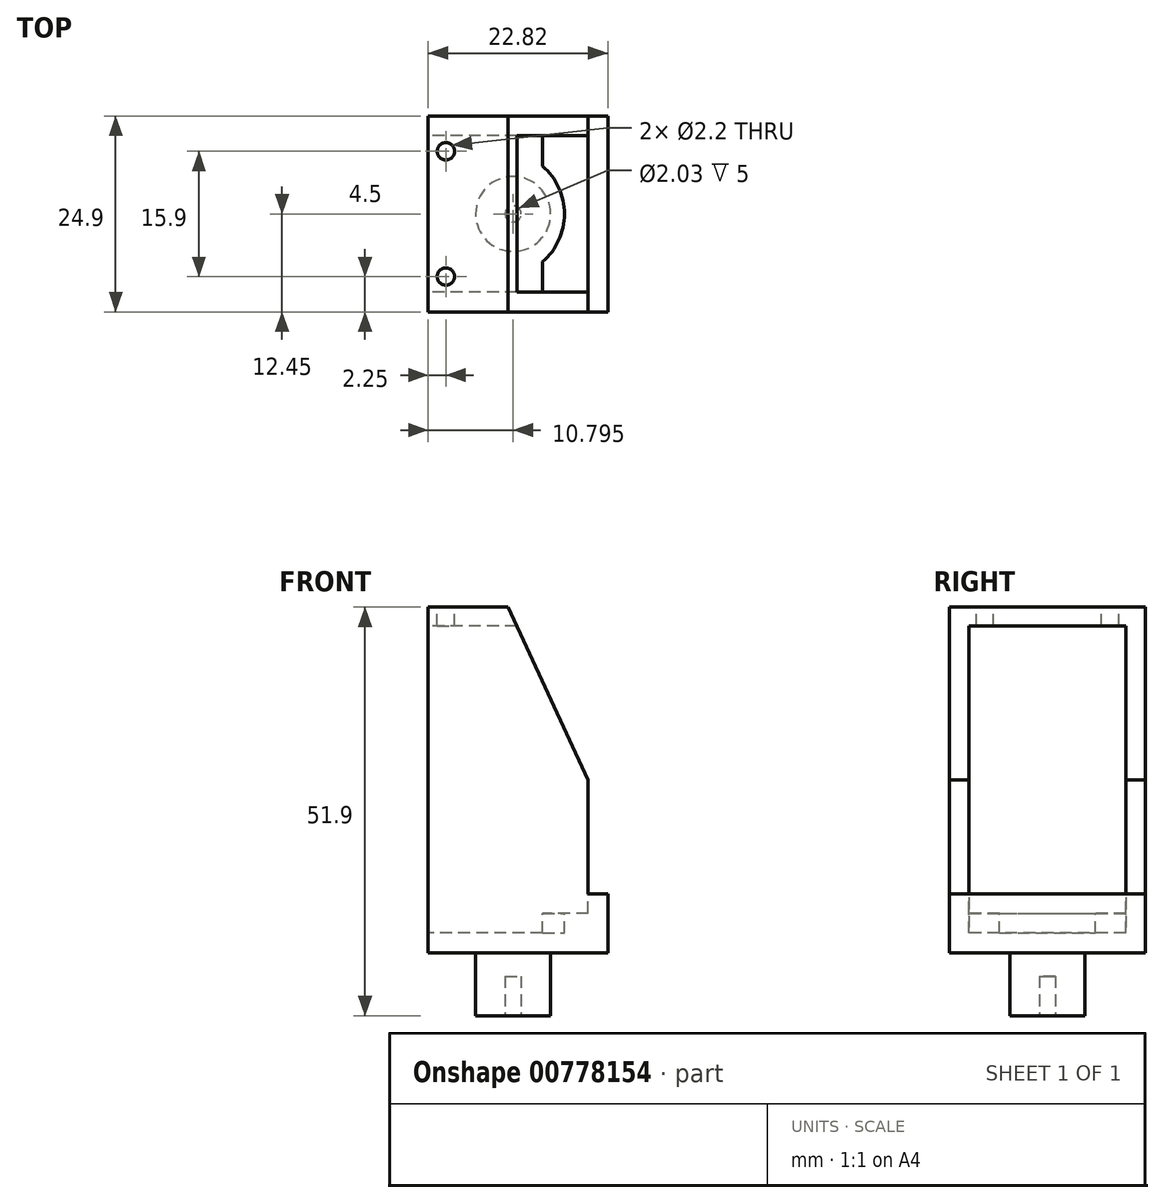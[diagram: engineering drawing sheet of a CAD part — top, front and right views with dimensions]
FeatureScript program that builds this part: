
annotation { "Feature Type Name" : "Feature", "Feature Type Description" : "" }
export const myFeature = defineFeature(function(context is Context, id is Id, definition is map)
    precondition{}
    {
        {
            var Q0;
            Q0=qCreatedBy(makeId("Front.planeOp"),FACE);
            var sketch = newSketch(context, id + "F0", { "sketchPlane" : qUnion([Q0])});
            skLineSegment(sketch, "E0.bottom", {"start": v(0, 21.95) * mm, "end": v(-10.16, 21.95) * mm});
            skLineSegment(sketch, "E0.top", {"start": v(10.16, -21.95) * mm, "end": v(-10.16, -21.95) * mm});
            skLineSegment(sketch, "E0.left", {"start": v(10.16, 0) * mm, "end": v(10.16, -21.95) * mm});
            skLineSegment(sketch, "E0.right", {"start": v(-10.16, 21.95) * mm, "end": v(-10.16, -21.95) * mm});
            skPoint(sketch, "E0.middle", {"position": v(0, 0) * mm});
            skLineSegment(sketch, "E1", {"start": v(0, 21.95) * mm, "end": v(10.16, 0) * mm});
            skPoint(sketch, "E2.orphan", {"position": v(10.16, 21.95) * mm});
            skSolve(sketch);
        }
        {
            var Q0;
            Q0 = qSketchRegion(id + "F0", true);
            extrude(context, id + "F1", {"entities" : qUnion([Q0]), "depth" : 24.9 * mm, "offsetDistance" : 25.4 * mm});
        }
        {
            var Q0;
            Q0=makeQuery(id+"F1.opExtrude","SWEPT_FACE",FACE,{"disambiguationData":[OSD([sQuery(id+"F0.wireOp",EDGE,"E0.right")])]});
            var sketch = newSketch(context, id + "F2", { "sketchPlane" : qUnion([Q0])});
            skLineSegment(sketch, "E3.bottom", {"start": v(2.5, 19.55) * mm, "end": v(22.4, 19.55) * mm});
            skLineSegment(sketch, "E3.top", {"start": v(2.5, -16.95) * mm, "end": v(22.4, -16.95) * mm});
            skLineSegment(sketch, "E3.left", {"start": v(2.5, 19.55) * mm, "end": v(2.5, -16.95) * mm});
            skLineSegment(sketch, "E3.right", {"start": v(22.4, 19.55) * mm, "end": v(22.4, -16.95) * mm});
            skSolve(sketch);
        }
        {
            var Q0;
            Q0 = qSketchRegion(id + "F2", true);
            extrude(context, id + "F3", {"entities" : qUnion([Q0]), "operationType" : NewBodyOperationType.REMOVE, "oppositeDirection" : true, "depth" : 25.4 * mm, "offsetDistance" : 25.4 * mm});
        }
        {
            var Q0;
            Q0=makeQuery(id+"F1.opExtrude","SWEPT_FACE",FACE,{"disambiguationData":[OSD([sQuery(id+"F0.wireOp",EDGE,"E0.right")])]});
            var sketch = newSketch(context, id + "F4", { "sketchPlane" : qUnion([Q0])});
            skLineSegment(sketch, "E4.bottom", {"start": v(0, 21.95) * mm, "end": v(24.9, 21.95) * mm});
            skLineSegment(sketch, "E4.top", {"start": v(0, 16.95) * mm, "end": v(24.9, 16.95) * mm});
            skLineSegment(sketch, "E4.left", {"start": v(0, 21.95) * mm, "end": v(0, 16.95) * mm});
            skLineSegment(sketch, "E4.right", {"start": v(24.9, 21.95) * mm, "end": v(24.9, 16.95) * mm});
            skLineSegment(sketch, "E5.bottom", {"start": v(0, -21.95) * mm, "end": v(24.9, -21.95) * mm});
            skLineSegment(sketch, "E5.top", {"start": v(0, -14.45) * mm, "end": v(24.9, -14.45) * mm});
            skLineSegment(sketch, "E5.left", {"start": v(0, -21.95) * mm, "end": v(0, -14.45) * mm});
            skLineSegment(sketch, "E5.right", {"start": v(24.9, -21.95) * mm, "end": v(24.9, -14.45) * mm});
            skSolve(sketch);
        }
        {
            var Q0;
            Q0 = qSketchRegion(id + "F4", true);
            extrude(context, id + "F5", {"entities" : qUnion([Q0]), "operationType" : NewBodyOperationType.ADD, "depth" : 2.5 * mm, "offsetDistance" : 25.4 * mm});
        }
        {
            var Q0;
            Q0=makeQuery(id+"F3.boolean.opBoolean","COPY",FACE,{"derivedFrom":makeQuery(id+"F3.opExtrude","SWEPT_FACE",FACE,{"disambiguationData":[OSD([sQuery(id+"F2.wireOp",EDGE,"E3.top")])]})});
            var sketch = newSketch(context, id + "F6", { "sketchPlane" : qUnion([Q0])});
            skLineSegment(sketch, "E6.bottom", {"start": v(10.16, -2.5) * mm, "end": v(4.36, -2.5) * mm});
            skLineSegment(sketch, "E6.top", {"start": v(10.16, -22.4) * mm, "end": v(4.36, -22.4) * mm});
            skLineSegment(sketch, "E6.left", {"start": v(10.16, -2.5) * mm, "end": v(10.16, -22.4) * mm});
            skLineSegment(sketch, "E6.right", {"start": v(4.36, -2.5) * mm, "end": v(4.36, -6.37) * mm});
            skPoint(sketch, "E7", {"position": v(-0.84, -12.45) * mm});
            skPoint(sketch, "E7.positionSnap0", {"position": v(4.36, -12.45) * mm});
            skArc(sketch, "E8", {"start": v(4.36, -6.37) * mm, "mid": v(7.16, -12.45) * mm, "end": v(4.36, -18.53) * mm});
            skLineSegment(sketch, "E9.trimOffspring", {"start": v(4.36, -18.53) * mm, "end": v(4.36, -22.4) * mm});
            skSolve(sketch);
        }
        {
            var Q0;
            {var subQ3=sQuery(id+"F6.wireOp",EDGE,"E6.right");Q0=makeQuery(id+"F6.imprint","IMPRINT",FACE,{"disambiguationData":[TD([[makeQuery(id+"F6.imprint","IMPRINT",EDGE,{"derivedFrom":subQ3}),-1.0]])]});}
            extrude(context, id + "F7", {"entities" : qUnion([Q0]), "operationType" : NewBodyOperationType.REMOVE, "oppositeDirection" : true, "depth" : 2.5 * mm, "offsetDistance" : 25.4 * mm});
        }
        {
            var Q0;
            Q0=makeQuery(id+"F5.boolean.opBoolean","MERGE",FACE,{"derivedFrom":[makeQuery(id+"F1.opExtrude","SWEPT_FACE",FACE,{"disambiguationData":[OSD([sQuery(id+"F0.wireOp",EDGE,"E0.bottom")])]}),makeQuery(id+"F5.opExtrude","SWEPT_FACE",FACE,{"disambiguationData":[OSD([sQuery(id+"F4.wireOp",EDGE,"E4.bottom")])]})]});
            var sketch = newSketch(context, id + "F8", { "sketchPlane" : qUnion([Q0])});
            skCircle(sketch, "E10", {"center": v(-7.9, -4.5) * mm, "radius": 1.1 * mm});
            skLineSegment(sketch, "E11", {"start": v(-31.79, -12.45) * mm, "end": v(21.26, -12.45) * mm, "construction": true});
            skPoint(sketch, "E11.startSnap0", {"position": v(-12.66, -12.45) * mm});
            skCircle(sketch, "E12.MirrorC", {"center": v(-7.9, -20.4) * mm, "radius": 1.1 * mm});
            skSolve(sketch);
        }
        {
            var Q0;
            Q0 = qSketchRegion(id + "F8", true);
            extrude(context, id + "F9", {"entities" : qUnion([Q0]), "operationType" : NewBodyOperationType.REMOVE, "oppositeDirection" : true, "depth" : 25.4 * mm, "offsetDistance" : 25.4 * mm});
        }
        {
            var Q0;
            Q0=makeQuery(id+"F5.boolean.opBoolean","MERGE",FACE,{"derivedFrom":[makeQuery(id+"F1.opExtrude","SWEPT_FACE",FACE,{"disambiguationData":[OSD([sQuery(id+"F0.wireOp",EDGE,"E0.top")])]}),makeQuery(id+"F5.opExtrude","SWEPT_FACE",FACE,{"disambiguationData":[OSD([sQuery(id+"F4.wireOp",EDGE,"E5.bottom")])]})]});
            var sketch = newSketch(context, id + "F10", { "sketchPlane" : qUnion([Q0])});
            skCircle(sketch, "E13", {"center": v(0.64, 12.45) * mm, "radius": 4.76 * mm});
            skLineSegment(sketch, "E14", {"start": v(-12.66, 12.45) * mm, "end": v(10.16, 12.45) * mm, "construction": true});
            skSolve(sketch);
        }
        {
            var Q0;
            Q0 = qSketchRegion(id + "F10", true);
            extrude(context, id + "F11", {"entities" : qUnion([Q0]), "operationType" : NewBodyOperationType.ADD, "depth" : 8 * mm, "offsetDistance" : 25.4 * mm});
        }
        {
            var Q0;
            Q0=makeQuery(id+"F11.opExtrude","CAP_FACE",FACE,{"disambiguationData":[OSD([sQuery(id+"F10.wireOp",EDGE,"E13")])],"isStart":false});
            var sketch = newSketch(context, id + "F12", { "sketchPlane" : qUnion([Q0])});
            skCircle(sketch, "E15", {"center": v(0.64, 12.45) * mm, "radius": 1.02 * mm});
            skSolve(sketch);
        }
        {
            var Q0;
            Q0 = qSketchRegion(id + "F12", true);
            extrude(context, id + "F13", {"entities" : qUnion([Q0]), "operationType" : NewBodyOperationType.REMOVE, "oppositeDirection" : true, "depth" : 5 * mm, "offsetDistance" : 25.4 * mm});
        }
        {
            var Q0;
            Q0=makeQuery(id+"F5.boolean.opBoolean","MERGE",FACE,{"derivedFrom":[makeQuery(id+"F1.opExtrude","CAP_FACE",FACE,{"disambiguationData":[OSD([sQuery(id+"F0.wireOp",EDGE,"E0.bottom"),sQuery(id+"F0.wireOp",EDGE,"E0.top"),sQuery(id+"F0.wireOp",EDGE,"E0.left"),sQuery(id+"F0.wireOp",EDGE,"E0.right"),sQuery(id+"F0.wireOp",EDGE,"E1")])],"isStart":false}),makeQuery(id+"F5.opExtrude","SWEPT_FACE",FACE,{"disambiguationData":[OSD([sQuery(id+"F4.wireOp",EDGE,"E4.right")])]}),makeQuery(id+"F5.opExtrude","SWEPT_FACE",FACE,{"disambiguationData":[OSD([sQuery(id+"F4.wireOp",EDGE,"E5.right")])]})]});
            var sketch = newSketch(context, id + "F14", { "sketchPlane" : qUnion([Q0])});
            skLineSegment(sketch, "E16.bottom", {"start": v(-12.66, -14.45) * mm, "end": v(-10.16, -14.45) * mm});
            skLineSegment(sketch, "E16.top", {"start": v(-12.66, -21.95) * mm, "end": v(-10.16, -21.95) * mm});
            skLineSegment(sketch, "E16.left", {"start": v(-12.66, -14.45) * mm, "end": v(-12.66, -21.95) * mm});
            skLineSegment(sketch, "E16.right", {"start": v(-10.16, -14.45) * mm, "end": v(-10.16, -21.95) * mm});
            skLineSegment(sketch, "E17.bottom", {"start": v(-12.66, 16.95) * mm, "end": v(-10.16, 16.95) * mm});
            skLineSegment(sketch, "E17.top", {"start": v(-12.66, 21.95) * mm, "end": v(-10.16, 21.95) * mm});
            skLineSegment(sketch, "E17.left", {"start": v(-12.66, 16.95) * mm, "end": v(-12.66, 21.95) * mm});
            skLineSegment(sketch, "E17.right", {"start": v(-10.16, 16.95) * mm, "end": v(-10.16, 21.95) * mm});
            skSolve(sketch);
        }
        {
            var Q0;
            Q0 = qSketchRegion(id + "F14", true);
            extrude(context, id + "F15", {"entities" : qUnion([Q0]), "operationType" : NewBodyOperationType.REMOVE, "oppositeDirection" : true, "depth" : 25.4 * mm, "offsetDistance" : 25.4 * mm});
        }
        {
            var Q0;
            Q0=makeQuery(id+"F1.opExtrude","SWEPT_FACE",FACE,{"disambiguationData":[OSD([sQuery(id+"F0.wireOp",EDGE,"E0.left")])]});
            var sketch = newSketch(context, id + "F16", { "sketchPlane" : qUnion([Q0])});
            skLineSegment(sketch, "E18.bottom", {"start": v(0, -21.95) * mm, "end": v(-24.9, -21.95) * mm});
            skLineSegment(sketch, "E18.top", {"start": v(0, -14.45) * mm, "end": v(-24.9, -14.45) * mm});
            skLineSegment(sketch, "E18.left", {"start": v(0, -21.95) * mm, "end": v(0, -14.45) * mm});
            skLineSegment(sketch, "E18.right", {"start": v(-24.9, -21.95) * mm, "end": v(-24.9, -14.45) * mm});
            skSolve(sketch);
        }
        {
            var Q0;
            Q0 = qSketchRegion(id + "F16", true);
            extrude(context, id + "F17", {"entities" : qUnion([Q0]), "operationType" : NewBodyOperationType.ADD, "depth" : 2.5 * mm, "offsetDistance" : 25.4 * mm});
        }
    });
